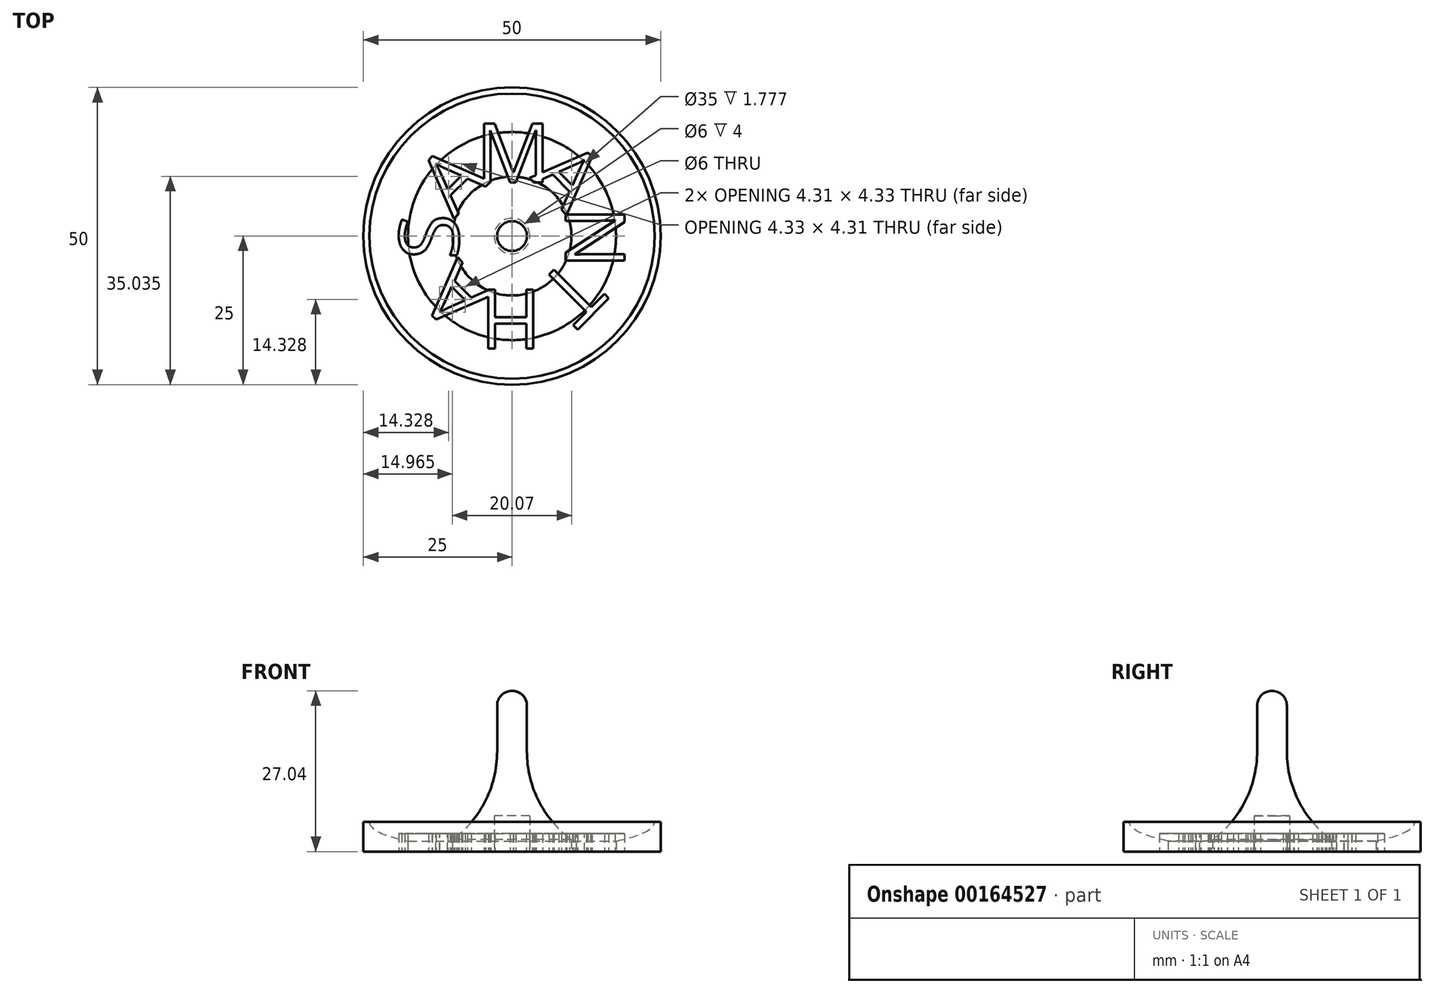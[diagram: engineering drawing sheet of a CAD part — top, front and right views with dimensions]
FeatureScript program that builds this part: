
annotation { "Feature Type Name" : "Feature", "Feature Type Description" : "" }
export const myFeature = defineFeature(function(context is Context, id is Id, definition is map)
    precondition{}
    {
        {
            var Q0;
            Q0=qCreatedBy(makeId("Top.planeOp"),FACE);
            var sketch = newSketch(context, id + "F0", { "sketchPlane" : qUnion([Q0])});
            skCircle(sketch, "E0", {"center": v(0, 0) * mm, "radius": 17.5 * mm});
            skCircle(sketch, "E1", {"center": v(0, 0) * mm, "radius": 25 * mm});
            skSolve(sketch);
        }
        {
            var Q0;
            Q0=makeQuery(id+"F0.imprint","IMPRINT",FACE,{"disambiguationData":[TD([[makeQuery(id+"F0.imprint","IMPRINT",EDGE,{"derivedFrom":sQuery(id+"F0.wireOp",EDGE,"E0")}),-1.0]])]});
            extrude(context, id + "F1", {"entities" : qUnion([Q0]), "depth" : 5 * mm});
        }
        {
            var Q0;
            Q0=qCreatedBy(makeId("Front.planeOp"),FACE);
            var sketch = newSketch(context, id + "F2", { "sketchPlane" : qUnion([Q0])});
            skEllipse(sketch, "E2", {"center": v(0, 4.92) * mm, "majorRadius": 23.98 * mm, "minorRadius": 4.6 * mm, "majorAxis": v(-1, 0)});
            skLineSegment(sketch, "E3", {"start": v(0, 9.52) * mm, "end": v(0, 0.32) * mm});
            skSolve(sketch);
        }
        {
            var Q0;
            {var subQ0=sQuery(id+"F2.wireOp",EDGE,"E3");Q0=makeQuery(id+"F2.imprint","IMPRINT",FACE,{"disambiguationData":[TD([[makeQuery(id+"F2.imprint","IMPRINT",EDGE,{"derivedFrom":subQ0}),-1.0]])]});}
            var Q1;
            Q1=sQuery(id+"F2.wireOp",EDGE,"E3");
            revolve(context, id + "F3", {"operationType" : NewBodyOperationType.REMOVE, "entities" : qUnion([Q0]), "axis" : qUnion([Q1]), "revolveType" : RevolveType.FULL, "oppositeDirection" : true});
        }
        {
            var Q0;
            Q0=qCreatedBy(makeId("Top.planeOp"),FACE);
            var sketch = newSketch(context, id + "F4", { "sketchPlane" : qUnion([Q0])});
            skCircle(sketch, "E4", {"center": v(0, 0) * mm, "radius": 10 * mm});
            skSolve(sketch);
        }
        {
            var Q0;
            Q0 = qSketchRegion(id + "F4", true);
            extrude(context, id + "F5", {"entities" : qUnion([Q0]), "depth" : 2 * mm});
        }
        {
            var Q0;
            Q0=qCreatedBy(makeId("Top.planeOp"),FACE);
            var sketch = newSketch(context, id + "F6", { "sketchPlane" : qUnion([Q0])});
            skCircle(sketch, "E5", {"center": v(0, 0) * mm, "radius": 9 * mm, "construction": true});
            skText(sketch, "E6", { "text": "S", "fontName": "OpenSans-Regular.ttf"});
            skCircle(sketch, "E7", {"center": v(0, 0) * mm, "radius": 19 * mm, "construction": true});
            skText(sketch, "E8", { "text": "A", "fontName": "OpenSans-Regular.ttf"});
            skText(sketch, "E9", { "text": "A", "fontName": "OpenSans-Regular.ttf"});
            skText(sketch, "E10", { "text": "N", "fontName": "OpenSans-Regular.ttf"});
            skText(sketch, "E11", { "text": "T", "fontName": "OpenSans-Regular.ttf"});
            skText(sketch, "E12", { "text": "H", "fontName": "OpenSans-Regular.ttf"});
            skText(sketch, "E13", { "text": "A", "fontName": "OpenSans-Regular.ttf"});
            skText(sketch, "E14", { "text": "M", "fontName": "OpenSans-Regular.ttf"});
            const initialGuessF6  = {"E6": [-0.009, -0.00393, 0, 1, 0.01], "E8": [-0.00979, 0.00294, 0.7071, 0.7071, 0.01], "E9": [0.00294, 0.00979, 0.7071, -0.7071, 0.01], "E10": [0.009, 0.005, 0, -1, 0.01], "E11": [0.00935, -0.00337, -0.7071, -0.7071, 0.01], "E12": [0.0049, -0.009, -1, -0.00127, 0.01], "E13": [-0.00294, -0.00979, -0.7071, 0.7071, 0.01], "E14": [-0.00604, 0.009, 1, 0, 0.01]};
            skSetInitialGuess(sketch, initialGuessF6);
            skSolve(sketch);
        }
        {
            var Q0;
            Q0 = qSketchRegion(id + "F6", true);
            extrude(context, id + "F7", {"entities" : qUnion([Q0]), "depth" : 3 * mm});
        }
        {
            var Q0;
            Q0=qCreatedBy(makeId("Front.planeOp"),FACE);
            var sketch = newSketch(context, id + "F8", { "sketchPlane" : qUnion([Q0])});
            skLineSegment(sketch, "E15.bottom", {"start": v(10, 2) * mm, "end": v(-10, 2) * mm, "construction": true});
            skLineSegment(sketch, "E15.top", {"start": v(10, -2) * mm, "end": v(-10, -2) * mm, "construction": true});
            skLineSegment(sketch, "E15.left", {"start": v(10, 2) * mm, "end": v(10, -2) * mm, "construction": true});
            skLineSegment(sketch, "E15.right", {"start": v(-10, 2) * mm, "end": v(-10, -2) * mm, "construction": true});
            skCircle(sketch, "E16", {"center": v(0, 24.54) * mm, "radius": 2.5 * mm});
            skLineSegment(sketch, "E17.bottom", {"start": v(-2.5, 24.54) * mm, "end": v(2.5, 24.54) * mm});
            skLineSegment(sketch, "E17.top", {"start": v(-2.5, 16.84) * mm, "end": v(2.5, 16.84) * mm});
            skLineSegment(sketch, "E17.left", {"start": v(-2.5, 24.54) * mm, "end": v(-2.5, 16.84) * mm});
            skLineSegment(sketch, "E17.right", {"start": v(2.5, 24.54) * mm, "end": v(2.5, 16.84) * mm});
            skArc(sketch, "E18", {"start": v(-10, 2) * mm, "mid": v(-4.48, 8.52) * mm, "end": v(-2.5, 16.84) * mm});
            skLineSegment(sketch, "E19", {"start": v(0, 16.84) * mm, "end": v(0, 2) * mm});
            skLineSegment(sketch, "E20", {"start": v(0, 2) * mm, "end": v(-10, 2) * mm});
            skLineSegment(sketch, "E21", {"start": v(0, 16.84) * mm, "end": v(0, 27.04) * mm});
            skSolve(sketch);
        }
        {
            var Q0;
            {var subQ1=sQuery(id+"F8.wireOp",EDGE,"E16");var subQ3=sQuery(id+"F8.wireOp",EDGE,"E21");var subQ4=makeQuery(id+"F8.imprint","INTERSECT",VERTEX,{"disambiguationData":[OD(0.0)],"derivedFrom":[subQ1,subQ3]});Q0=makeQuery(id+"F8.imprint","IMPRINT",FACE,{"disambiguationData":[TD([[makeQuery(id+"F8.imprint","IMPRINT",EDGE,{"disambiguationData":[TD([[subQ4,1.0]])],"derivedFrom":subQ3}),1.0]])]});}
            var Q1;
            {var subQ1=sQuery(id+"F8.wireOp",EDGE,"E16");var subQ3=sQuery(id+"F8.wireOp",EDGE,"E21");var subQ4=makeQuery(id+"F8.imprint","INTERSECT",VERTEX,{"disambiguationData":[OD(1.0)],"derivedFrom":[subQ1,subQ3]});Q1=makeQuery(id+"F8.imprint","IMPRINT",FACE,{"disambiguationData":[TD([[makeQuery(id+"F8.imprint","IMPRINT",EDGE,{"disambiguationData":[TD([[subQ4,-1.0]])],"derivedFrom":subQ3}),1.0]])]});}
            var Q2;
            {var subQ0=sQuery(id+"F8.wireOp",EDGE,"E17.left");Q2=makeQuery(id+"F8.imprint","IMPRINT",FACE,{"disambiguationData":[TD([[makeQuery(id+"F8.imprint","IMPRINT",EDGE,{"derivedFrom":subQ0}),1.0]])]});}
            var Q3;
            {var subQ0=sQuery(id+"F8.wireOp",EDGE,"E18");Q3=makeQuery(id+"F8.imprint","IMPRINT",FACE,{"disambiguationData":[TD([[makeQuery(id+"F8.imprint","IMPRINT",EDGE,{"derivedFrom":subQ0}),-1.0]])]});}
            var Q4;
            Q4=sQuery(id+"F8.wireOp",EDGE,"E19");
            revolve(context, id + "F9", {"entities" : qUnion([Q0, Q1, Q2, Q3]), "axis" : qUnion([Q4]), "revolveType" : RevolveType.FULL});
        }
        {
            var Q0;
            Q0=qCreatedBy(makeId("Top.planeOp"),FACE);
            var sketch = newSketch(context, id + "F10", { "sketchPlane" : qUnion([Q0])});
            skCircle(sketch, "E22", {"center": v(0, 0) * mm, "radius": 3 * mm});
            skSolve(sketch);
        }
        {
            var Q0;
            Q0 = qSketchRegion(id + "F10", true);
            extrude(context, id + "F11", {"entities" : qUnion([Q0]), "operationType" : NewBodyOperationType.REMOVE, "depth" : 6 * mm});
        }
    });
